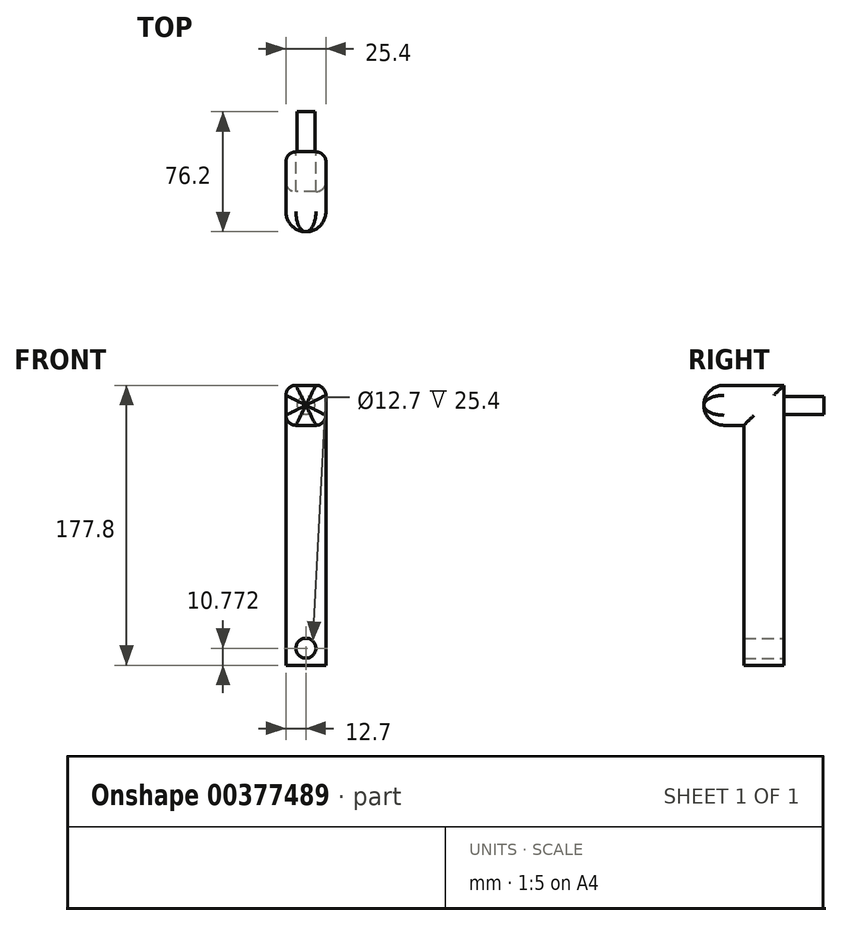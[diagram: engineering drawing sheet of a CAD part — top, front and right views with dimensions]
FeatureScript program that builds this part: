
annotation { "Feature Type Name" : "Feature", "Feature Type Description" : "" }
export const myFeature = defineFeature(function(context is Context, id is Id, definition is map)
    precondition{}
    {
        {
            var Q0;
            Q0=qCreatedBy(makeId("Front.planeOp"),FACE);
            var sketch = newSketch(context, id + "F0", { "sketchPlane" : qUnion([Q0])});
            skLineSegment(sketch, "E0", {"start": v(0, -86.2) * mm, "end": v(-12.7, -86.2) * mm});
            skLineSegment(sketch, "E1", {"start": v(-12.7, -86.2) * mm, "end": v(-12.7, 91.6) * mm});
            skLineSegment(sketch, "E2.MirrorCS", {"start": v(12.7, -86.2) * mm, "end": v(12.7, 91.6) * mm});
            skLineSegment(sketch, "E3.MirrorCS", {"start": v(0, -86.2) * mm, "end": v(12.7, -86.2) * mm});
            skLineSegment(sketch, "E4", {"start": v(12.7, 91.6) * mm, "end": v(-12.7, 91.6) * mm});
            skSolve(sketch);
        }
        {
            var Q0;
            Q0 = qSketchRegion(id + "F0", true);
            extrude(context, id + "F1", {"entities" : qUnion([Q0]), "depth" : 25.4 * mm});
        }
        {
            var Q0;
            Q0=makeQuery(id+"F1.opExtrude","SWEPT_FACE",FACE,{"disambiguationData":[OSD([sQuery(id+"F0.wireOp",EDGE,"E1")])]});
            var sketch = newSketch(context, id + "F2", { "sketchPlane" : qUnion([Q0])});
            skLineSegment(sketch, "E5", {"start": v(25.4, 91.6) * mm, "end": v(50.8, 91.6) * mm});
            skLineSegment(sketch, "E6", {"start": v(50.8, 91.6) * mm, "end": v(50.8, 66.2) * mm});
            skLineSegment(sketch, "E7", {"start": v(50.8, 66.2) * mm, "end": v(25.4, 66.2) * mm});
            skSolve(sketch);
        }
        {
            var Q0;
            Q0=makeQuery(id+"F1.opExtrude","CAP_FACE",FACE,{"disambiguationData":[OSD([sQuery(id+"F0.wireOp",EDGE,"E0"),sQuery(id+"F0.wireOp",EDGE,"E1"),sQuery(id+"F0.wireOp",EDGE,"E2.MirrorCS"),sQuery(id+"F0.wireOp",EDGE,"E3.MirrorCS"),sQuery(id+"F0.wireOp",EDGE,"E4")])],"isStart":true});
            var sketch = newSketch(context, id + "F3", { "sketchPlane" : qUnion([Q0])});
            skLineSegment(sketch, "E8", {"start": v(0, 91.6) * mm, "end": v(0, 78.9) * mm});
            skCircle(sketch, "E9", {"center": v(0, 78.9) * mm, "radius": 5.72 * mm});
            skSolve(sketch);
        }
        {
            var Q0;
            Q0 = qSketchRegion(id + "F3", true);
            extrude(context, id + "F4", {"entities" : qUnion([Q0]), "operationType" : NewBodyOperationType.ADD, "depth" : 25.4 * mm});
        }
        {
            var Q0;
            Q0 = qSketchRegion(id + "F2", true);
            var Q1;
            {var subQ0=sQuery(id+"F2.wireOp",EDGE,"E5");Q1=makeQuery(id+"F2.imprint","IMPRINT",FACE,{"disambiguationData":[TD([[makeQuery(id+"F2.imprint","IMPRINT",EDGE,{"derivedFrom":subQ0}),-1.0]])]});}
            extrude(context, id + "F5", {"entities" : qUnion([Q0, Q1]), "operationType" : NewBodyOperationType.ADD, "depth" : -25.4 * mm});
        }
        {
            var Q0;
            Q0=makeQuery(id+"F1.opExtrude","CAP_EDGE",EDGE,{"disambiguationData":[OSD([sQuery(id+"F0.wireOp",EDGE,"E2.MirrorCS")])],"isStart":false});
            var Q1;
            Q1=makeQuery(id+"F1.opExtrude","CAP_EDGE",EDGE,{"disambiguationData":[OSD([sQuery(id+"F0.wireOp",EDGE,"E1")])],"isStart":true});
            var Q2;
            Q2=makeQuery(id+"F1.opExtrude","CAP_EDGE",EDGE,{"disambiguationData":[OSD([sQuery(id+"F0.wireOp",EDGE,"E2.MirrorCS")])],"isStart":true});
            var Q3;
            Q3=makeQuery(id+"F1.opExtrude","CAP_EDGE",EDGE,{"disambiguationData":[OSD([sQuery(id+"F0.wireOp",EDGE,"E1")])],"isStart":false});
            var Q4;
            Q4=makeQuery(id+"F5.boolean.opBoolean","MERGE",EDGE,{"derivedFrom":[makeQuery(id+"F1.opExtrude","SWEPT_EDGE",EDGE,{"disambiguationData":[OSD([sQuery(id+"F0.wireOp",EDGE,"E1"),sQuery(id+"F0.wireOp",EDGE,"E4")])]}),makeQuery(id+"F5.opExtrude","CAP_EDGE",EDGE,{"disambiguationData":[OSD([sQuery(id+"F2.wireOp",EDGE,"E5")])],"isStart":true})]});
            var Q5;
            Q5=makeQuery(id+"F5.boolean.opBoolean","MERGE",EDGE,{"derivedFrom":[makeQuery(id+"F1.opExtrude","SWEPT_EDGE",EDGE,{"disambiguationData":[OSD([sQuery(id+"F0.wireOp",EDGE,"E2.MirrorCS"),sQuery(id+"F0.wireOp",EDGE,"E4")])]}),makeQuery(id+"F5.opExtrude","CAP_EDGE",EDGE,{"disambiguationData":[OSD([sQuery(id+"F2.wireOp",EDGE,"E5")])],"isStart":false})]});
            var Q6;
            Q6=makeQuery(id+"F5.opExtrude","CAP_EDGE",EDGE,{"disambiguationData":[OSD([sQuery(id+"F2.wireOp",EDGE,"E7")])],"isStart":true});
            var Q7;
            Q7=makeQuery(id+"F5.opExtrude","CAP_EDGE",EDGE,{"disambiguationData":[OSD([sQuery(id+"F2.wireOp",EDGE,"E7")])],"isStart":false});
            fillet(context, id + "F6", {"entities" : qUnion([Q0, Q1, Q2, Q3, Q4, Q5, Q6, Q7]), "radius" : 6.35 * mm, "tangentPropagation" : true, "allowEdgeOverflow" : false});
        }
        {
            var Q0;
            Q0=makeQuery(id+"F5.opExtrude","SWEPT_EDGE",EDGE,{"disambiguationData":[OSD([sQuery(id+"F2.wireOp",EDGE,"E6"),sQuery(id+"F2.wireOp",EDGE,"E7")])]});
            fillet(context, id + "F7", {"entities" : qUnion([Q0]), "radius" : 12.7 * mm, "tangentPropagation" : true, "allowEdgeOverflow" : false});
        }
        {
            var Q0;
            Q0=makeQuery(id+"F1.opExtrude","CAP_FACE",FACE,{"disambiguationData":[OSD([sQuery(id+"F0.wireOp",EDGE,"E0"),sQuery(id+"F0.wireOp",EDGE,"E1"),sQuery(id+"F0.wireOp",EDGE,"E2.MirrorCS"),sQuery(id+"F0.wireOp",EDGE,"E3.MirrorCS"),sQuery(id+"F0.wireOp",EDGE,"E4")])],"isStart":true});
            var sketch = newSketch(context, id + "F8", { "sketchPlane" : qUnion([Q0])});
            skLineSegment(sketch, "E10", {"start": v(0, 0) * mm, "end": v(0, -86.2) * mm});
            skLineSegment(sketch, "E11", {"start": v(0, -86.2) * mm, "end": v(0, -43.1) * mm});
            skLineSegment(sketch, "E12", {"start": v(0, -43.1) * mm, "end": v(0, -64.64) * mm});
            skLineSegment(sketch, "E13", {"start": v(0, -64.64) * mm, "end": v(0, -86.2) * mm});
            skLineSegment(sketch, "E14", {"start": v(0, -86.2) * mm, "end": v(0, -75.42) * mm});
            skSolve(sketch);
        }
        {
            var Q0;
            Q0=sQuery(id+"F8.wireOp",VERTEX,"E14.end");
            var Q1;
            Q1=makeQuery(id+"F1.opExtrude","SWEPT_BODY",BODY,{"disambiguationData":[OSD([sQuery(id+"F0.wireOp",EDGE,"E0"),sQuery(id+"F0.wireOp",EDGE,"E1"),sQuery(id+"F0.wireOp",EDGE,"E2.MirrorCS"),sQuery(id+"F0.wireOp",EDGE,"E3.MirrorCS"),sQuery(id+"F0.wireOp",EDGE,"E4")])]});
            hole(context, id + "F9", {"style" : HoleStyle.SIMPLE, "endStyle" : HoleEndStyle.BLIND, "holeDiameter" : 12.7 * mm, "holeDepth" : 254 * mm, "tappedDepth" : 12.7 * mm, "tapClearance" : 3, "locations" : qUnion([Q0]), "scope" : qUnion([Q1])});
        }
    });
